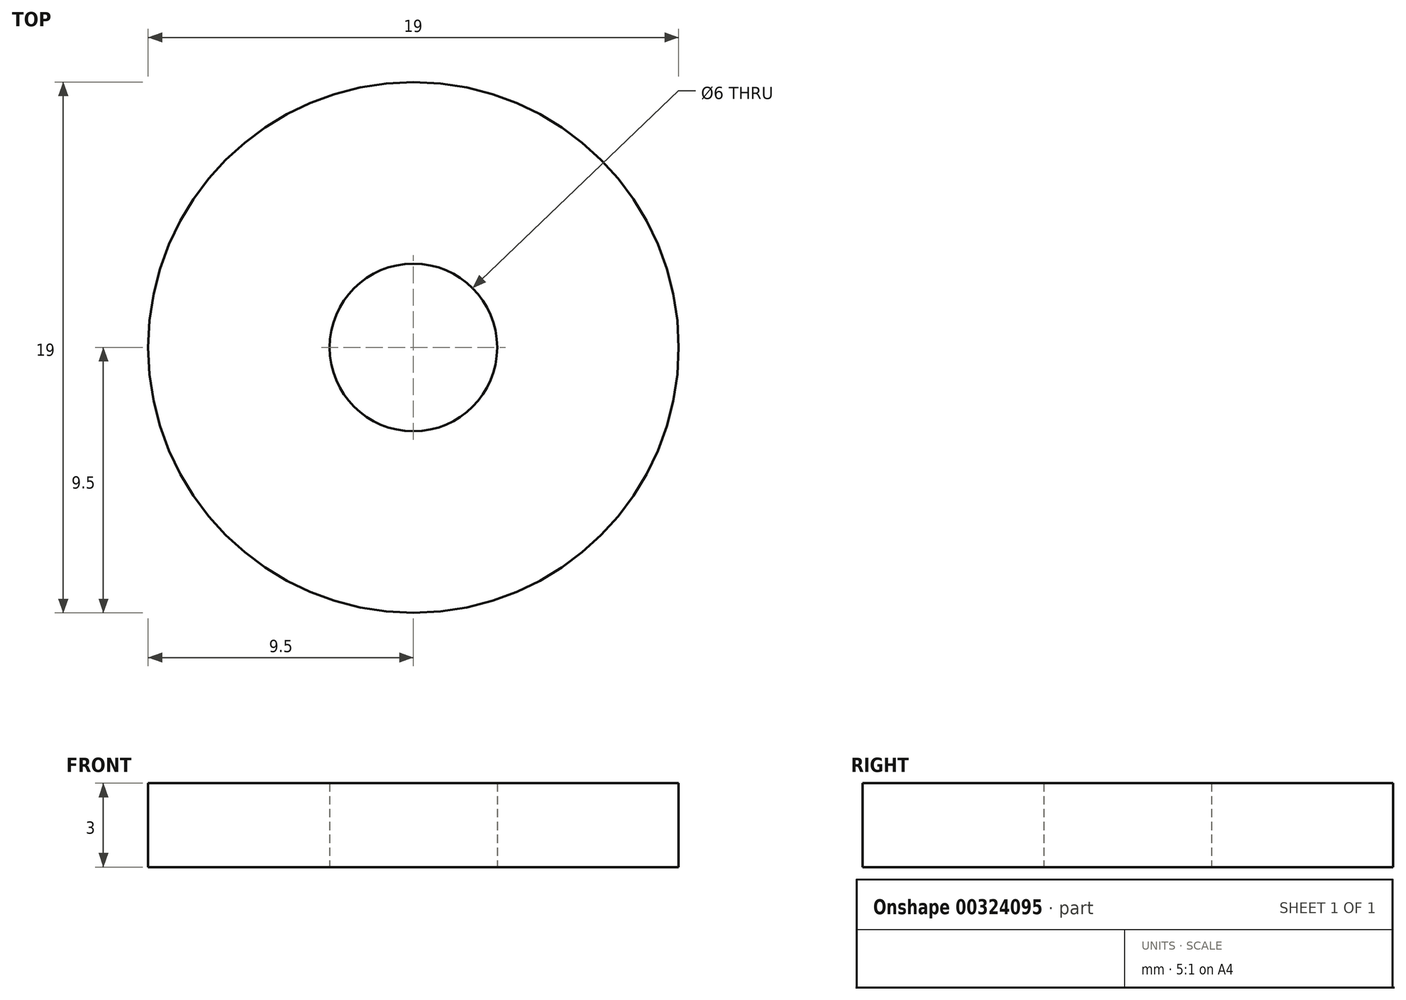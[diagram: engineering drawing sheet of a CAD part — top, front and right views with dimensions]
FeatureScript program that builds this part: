
annotation { "Feature Type Name" : "Feature", "Feature Type Description" : "" }
export const myFeature = defineFeature(function(context is Context, id is Id, definition is map)
    precondition{}
    {
        {
            var Q0;
            Q0=qCreatedBy(makeId("Top.planeOp"),FACE);
            var sketch = newSketch(context, id + "F0", { "sketchPlane" : qUnion([Q0])});
            skCircle(sketch, "E0", {"center": v(0, 0) * mm, "radius": 9.5 * mm});
            skCircle(sketch, "E1", {"center": v(0, 0) * mm, "radius": 3 * mm});
            skSolve(sketch);
        }
        {
            var Q0;
            Q0=makeQuery(id+"F0.imprint","IMPRINT",FACE,{"disambiguationData":[TD([[makeQuery(id+"F0.imprint","IMPRINT",EDGE,{"derivedFrom":sQuery(id+"F0.wireOp",EDGE,"E0")}),1.0]])]});
            extrude(context, id + "F1", {"entities" : qUnion([Q0]), "depth" : 3 * mm, "offsetDistance" : 25 * mm});
        }
    });
